# Revit family: Cleverfit Exit_R16
name_source: partatom
category: Lighting Fixtures
revit_build: Autodesk Revit LT 2016 (Build: 20150220_1215(x64)
units: mm (PartAtom-declared; Revit-internal decimal feet)

## family parameters
Always vertical = Yes
Cut with Voids When Loaded = No
Light Source = Yes
Part Type = Normal
Room Calculation Point = No
Round Connector Dimension = Use Diameter
Shared = No
Work Plane-Based = Yes

## types (2) — shared parameters
Annotation Direction = Exit_Annotation : Double Sided Direction Exit Luminaire
Ballast = Electronic
Charging Method = Dual Rate
Color Filter = 16777215
Default Elevation = 1219 mm
Description = Theatre Cleverfit Exit
Diffuser = All directional inserts included in the box
Dimming Lamp Color Temperature Shift = <None>
Double Sided = Yes
Emit Shape Visible in Rendering = No
Emit from Circle Diameter = 355 mm
Height = 215 mm
Lamp = 6 x high intensity, low energy LED, surface mounted onto a replaceable lamp bar - 100,000hour
Length = 355 mm
Manufacturer = Clevertronics
Model = ZCFLED
Mounting = Wall, Ceiling Single-Sided & Ceiling Double-Sided
Operating Mode = Maintained
Operating Voltage = 240 V
Sign Direction = Sign : Exit
Single Sided = Yes
Tilt Angle = 90.00°
Viewing Distance = 24000 mm  [stored 78.7402 ft]
Wattage Comments = Standby
Width = 80 mm  [stored 0.262467 ft]

## per-type parameters (varying)
| type | AS2293 | Apparent Load | Photometric Web File | Power Consumption | Testing System |
| ZCFLED | C0=E1.6 C90=E1.6 | 4 W | Premium Cleverfit LED Exit Zoneworks.ies | 4 W | Zoneworks Computerised Testing |
| ECFLED | C0=E2.5  C90=E2 | 1 W | ll17785 - ECFLED-A5S Nichia NSSW157AT.ies | 1 W | Manual Test Switch |

note: [stored X ft] marks values corroborated as IEEE doubles in the binary element streams (Revit-internal decimal feet)

## geometry (parser evidence)
native form markers: Sweep x4
no freeform markers — native parametric forms only
